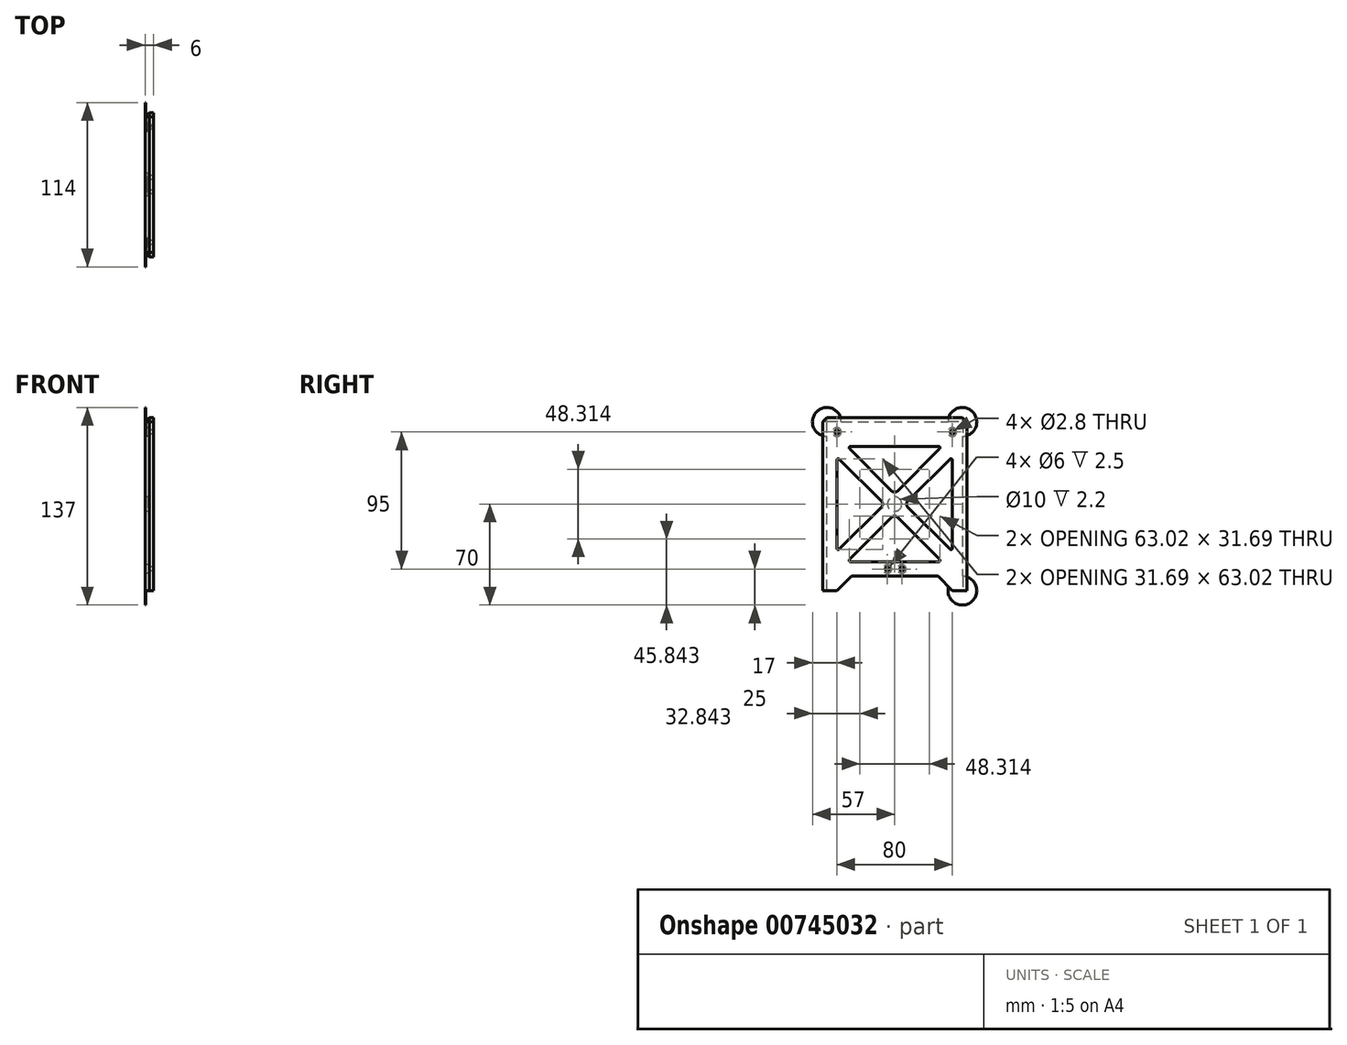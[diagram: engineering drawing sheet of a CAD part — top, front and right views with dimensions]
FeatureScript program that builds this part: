
annotation { "Feature Type Name" : "Feature", "Feature Type Description" : "" }
export const myFeature = defineFeature(function(context is Context, id is Id, definition is map)
    precondition{}
    {
        {
            var Q0;
            Q0=qCreatedBy(makeId("Right.planeOp"),FACE);
            var sketch = newSketch(context, id + "F0", { "sketchPlane" : qUnion([Q0])});
            skLineSegment(sketch, "E0.bottom", {"start": v(50, -60) * mm, "end": v(40.05, -60) * mm});
            skLineSegment(sketch, "E0.top", {"start": v(50, 60) * mm, "end": v(-50, 60) * mm});
            skLineSegment(sketch, "E0.left", {"start": v(50, -60) * mm, "end": v(50, 60) * mm});
            skLineSegment(sketch, "E0.right", {"start": v(-50, -60) * mm, "end": v(-50, 60) * mm});
            skPoint(sketch, "E0.middle", {"position": v(0, 0) * mm});
            skLineSegment(sketch, "E1.bottom", {"start": v(40, -40) * mm, "end": v(-32.93, -40) * mm});
            skLineSegment(sketch, "E1.top", {"start": v(32.93, 40) * mm, "end": v(-32.93, 40) * mm});
            skLineSegment(sketch, "E1.left", {"start": v(40, -40) * mm, "end": v(40, 32.93) * mm});
            skLineSegment(sketch, "E1.right", {"start": v(-40, -32.93) * mm, "end": v(-40, 32.93) * mm});
            skLineSegment(sketch, "E2.trimOffspring", {"start": v(-40, -60) * mm, "end": v(-50, -60) * mm});
            skLineSegment(sketch, "E3", {"start": v(30.05, -50) * mm, "end": v(40.05, -60) * mm});
            skLineSegment(sketch, "E4", {"start": v(30.05, -50) * mm, "end": v(-29.95, -50) * mm});
            skLineSegment(sketch, "E5", {"start": v(-29.95, -50) * mm, "end": v(-40, -60) * mm});
            skLineSegment(sketch, "E6", {"start": v(-40, -32.93) * mm, "end": v(-9.2, -2.12) * mm});
            skLineSegment(sketch, "E7.MirrorCS", {"start": v(-32.93, -40) * mm, "end": v(-2.12, -9.2) * mm});
            skLineSegment(sketch, "E8.trimOffspring", {"start": v(-40, 32.93) * mm, "end": v(-9.2, 2.12) * mm});
            skLineSegment(sketch, "E9.MirrorCS", {"start": v(-32.93, 40) * mm, "end": v(-2.12, 9.2) * mm});
            skLineSegment(sketch, "E10.trimOffspring", {"start": v(9.2, 2.12) * mm, "end": v(40, 32.93) * mm});
            skLineSegment(sketch, "E11.trimOffspring", {"start": v(2.12, -9.2) * mm, "end": v(32.93, -40) * mm});
            skLineSegment(sketch, "E12.trimOffspring", {"start": v(9.2, -2.12) * mm, "end": v(40, -32.93) * mm});
            skLineSegment(sketch, "E13.trimOffspring", {"start": v(2.12, 9.2) * mm, "end": v(32.93, 40) * mm});
            skPoint(sketch, "E14.visualSharp", {"position": v(0, 7.07) * mm});
            skArc(sketch, "E14.filletArc", {"start": v(-2.12, 9.2) * mm, "mid": v(0, 8.31) * mm, "end": v(2.12, 9.2) * mm});
            skPoint(sketch, "E15.visualSharp", {"position": v(0, -7.07) * mm});
            skArc(sketch, "E15.filletArc", {"start": v(2.12, -9.2) * mm, "mid": v(0, -8.31) * mm, "end": v(-2.12, -9.2) * mm});
            skPoint(sketch, "E16.visualSharp", {"position": v(7.07, 0) * mm});
            skArc(sketch, "E16.filletArc", {"start": v(9.2, 2.12) * mm, "mid": v(8.31, 0) * mm, "end": v(9.2, -2.12) * mm});
            skPoint(sketch, "E17.visualSharp", {"position": v(-7.07, 0) * mm});
            skArc(sketch, "E17.filletArc", {"start": v(-9.2, -2.12) * mm, "mid": v(-8.31, 0) * mm, "end": v(-9.2, 2.12) * mm});
            skLineSegment(sketch, "E18", {"start": v(81.83, 50) * mm, "end": v(-92.03, 50) * mm, "construction": true});
            skPoint(sketch, "E19", {"position": v(40, 50) * mm});
            skPoint(sketch, "E20", {"position": v(-40, 50) * mm});
            skSolve(sketch);
        }
        {
            var Q0;
            Q0=qSketchRegion(id+"F0",true);
            extrude(context, id + "F1", {"entities" : qUnion([Q0]), "depth" : 6 * mm, "offsetDistance" : 25 * mm});
        }
        {
            var Q0;
            Q0=makeQuery(id+"F1.opExtrude","SWEPT_EDGE",EDGE,{"disambiguationData":[OSD([sQuery(id+"F0.wireOp",EDGE,"E1.top"),sQuery(id+"F0.wireOp",EDGE,"E9.MirrorCS")])]});
            var Q1;
            Q1=makeQuery(id+"F1.opExtrude","SWEPT_EDGE",EDGE,{"disambiguationData":[OSD([sQuery(id+"F0.wireOp",EDGE,"E1.top"),sQuery(id+"F0.wireOp",EDGE,"E13.trimOffspring")])]});
            var Q2;
            Q2=makeQuery(id+"F1.opExtrude","SWEPT_EDGE",EDGE,{"disambiguationData":[OSD([sQuery(id+"F0.wireOp",EDGE,"E1.right"),sQuery(id+"F0.wireOp",EDGE,"E8.trimOffspring")])]});
            var Q3;
            Q3=makeQuery(id+"F1.opExtrude","SWEPT_EDGE",EDGE,{"disambiguationData":[OSD([sQuery(id+"F0.wireOp",EDGE,"E1.right"),sQuery(id+"F0.wireOp",EDGE,"E6")])]});
            var Q4;
            Q4=makeQuery(id+"F1.opExtrude","SWEPT_EDGE",EDGE,{"disambiguationData":[OSD([sQuery(id+"F0.wireOp",EDGE,"E1.bottom"),sQuery(id+"F0.wireOp",EDGE,"E7.MirrorCS")])]});
            var Q5;
            Q5=makeQuery(id+"F1.opExtrude","SWEPT_EDGE",EDGE,{"disambiguationData":[OSD([sQuery(id+"F0.wireOp",EDGE,"E1.left"),sQuery(id+"F0.wireOp",EDGE,"E10.trimOffspring")])]});
            var Q6;
            Q6=makeQuery(id+"F1.opExtrude","SWEPT_EDGE",EDGE,{"disambiguationData":[OSD([sQuery(id+"F0.wireOp",EDGE,"E1.left"),sQuery(id+"F0.wireOp",EDGE,"E12.trimOffspring")])]});
            var Q7;
            Q7=makeQuery(id+"F1.opExtrude","SWEPT_EDGE",EDGE,{"disambiguationData":[OSD([sQuery(id+"F0.wireOp",EDGE,"E1.bottom"),sQuery(id+"F0.wireOp",EDGE,"E11.trimOffspring")])]});
            fillet(context, id + "F2", {"entities" : qUnion([Q0, Q1, Q2, Q3, Q4, Q5, Q6, Q7]), "radius" : 1 * mm, "tangentPropagation" : true, "allowEdgeOverflow" : false});
        }
        {
            var Q0;
            Q0=sQuery(id+"F0.wireOp",VERTEX,"E20");
            var Q1;
            Q1=sQuery(id+"F0.wireOp",VERTEX,"E19");
            var Q2;
            Q2=makeQuery(id+"F1.opExtrude","SWEPT_BODY",BODY,{"disambiguationData":[OSD([sQuery(id+"F0.wireOp",EDGE,"E0.bottom"),sQuery(id+"F0.wireOp",EDGE,"E0.top"),sQuery(id+"F0.wireOp",EDGE,"E0.left"),sQuery(id+"F0.wireOp",EDGE,"E0.right"),sQuery(id+"F0.wireOp",EDGE,"E1.bottom"),sQuery(id+"F0.wireOp",EDGE,"E1.top"),sQuery(id+"F0.wireOp",EDGE,"E1.left"),sQuery(id+"F0.wireOp",EDGE,"E1.right"),sQuery(id+"F0.wireOp",EDGE,"E2.trimOffspring"),sQuery(id+"F0.wireOp",EDGE,"E3"),sQuery(id+"F0.wireOp",EDGE,"E4"),sQuery(id+"F0.wireOp",EDGE,"E5"),sQuery(id+"F0.wireOp",EDGE,"E6"),sQuery(id+"F0.wireOp",EDGE,"E7.MirrorCS"),sQuery(id+"F0.wireOp",EDGE,"E8.trimOffspring"),sQuery(id+"F0.wireOp",EDGE,"E9.MirrorCS"),sQuery(id+"F0.wireOp",EDGE,"E10.trimOffspring"),sQuery(id+"F0.wireOp",EDGE,"E11.trimOffspring"),sQuery(id+"F0.wireOp",EDGE,"E12.trimOffspring"),sQuery(id+"F0.wireOp",EDGE,"E13.trimOffspring"),sQuery(id+"F0.wireOp",EDGE,"E14.filletArc"),sQuery(id+"F0.wireOp",EDGE,"E15.filletArc"),sQuery(id+"F0.wireOp",EDGE,"E16.filletArc"),sQuery(id+"F0.wireOp",EDGE,"E17.filletArc")])]});
            hole(context, id + "F3", {"style" : HoleStyle.C_BORE, "endStyle" : HoleEndStyle.THROUGH, "oppositeDirection" : true, "holeDiameter" : 2.8 * mm, "cBoreDiameter" : 6 * mm, "cBoreDepth" : 2.5 * mm, "majorDiameter" : 5 * mm, "isTappedThrough" : true, "tappedDepth" : 6 * mm, "tapClearance" : 3, "locations" : qUnion([Q0, Q1]), "scope" : qUnion([Q2])});
        }
        {
            var Q0;
            Q0=makeQuery(id+"F1.opExtrude","CAP_FACE",FACE,{"disambiguationData":[OSD([sQuery(id+"F0.wireOp",EDGE,"E0.bottom"),sQuery(id+"F0.wireOp",EDGE,"E0.top"),sQuery(id+"F0.wireOp",EDGE,"E0.left"),sQuery(id+"F0.wireOp",EDGE,"E0.right"),sQuery(id+"F0.wireOp",EDGE,"E1.bottom"),sQuery(id+"F0.wireOp",EDGE,"E1.top"),sQuery(id+"F0.wireOp",EDGE,"E1.left"),sQuery(id+"F0.wireOp",EDGE,"E1.right"),sQuery(id+"F0.wireOp",EDGE,"E2.trimOffspring"),sQuery(id+"F0.wireOp",EDGE,"E3"),sQuery(id+"F0.wireOp",EDGE,"E4"),sQuery(id+"F0.wireOp",EDGE,"E5"),sQuery(id+"F0.wireOp",EDGE,"E6"),sQuery(id+"F0.wireOp",EDGE,"E7.MirrorCS"),sQuery(id+"F0.wireOp",EDGE,"E8.trimOffspring"),sQuery(id+"F0.wireOp",EDGE,"E9.MirrorCS"),sQuery(id+"F0.wireOp",EDGE,"E10.trimOffspring"),sQuery(id+"F0.wireOp",EDGE,"E11.trimOffspring"),sQuery(id+"F0.wireOp",EDGE,"E12.trimOffspring"),sQuery(id+"F0.wireOp",EDGE,"E13.trimOffspring"),sQuery(id+"F0.wireOp",EDGE,"E14.filletArc"),sQuery(id+"F0.wireOp",EDGE,"E15.filletArc"),sQuery(id+"F0.wireOp",EDGE,"E16.filletArc"),sQuery(id+"F0.wireOp",EDGE,"E17.filletArc")])],"isStart":true});
            var sketch = newSketch(context, id + "F4", { "sketchPlane" : qUnion([Q0])});
            skCircle(sketch, "E21", {"center": v(0, 0) * mm, "radius": 5 * mm});
            skSolve(sketch);
        }
        {
            var Q0;
            Q0=makeQuery(id+"F4.imprint","IMPRINT",FACE,{"disambiguationData":[TD([[makeQuery(id+"F4.imprint","IMPRINT",EDGE,{"derivedFrom":sQuery(id+"F4.wireOp",EDGE,"E21")}),1.0]])]});
            extrude(context, id + "F5", {"entities" : qUnion([Q0]), "operationType" : NewBodyOperationType.REMOVE, "oppositeDirection" : true, "depth" : 2.2 * mm, "offsetDistance" : 25 * mm});
        }
        {
            var Q0;
            {var subQ0=sQuery(id+"F0.wireOp",EDGE,"E0.left");var subQ1=sQuery(id+"F0.wireOp",EDGE,"E0.top");var subQ2=sQuery(id+"F0.wireOp",EDGE,"E0.right");var subQ3=sQuery(id+"F0.wireOp",EDGE,"E2.trimOffspring");var subQ4=sQuery(id+"F0.wireOp",EDGE,"E0.bottom");Q0=makeQuery(id+"F10.boolean.opBoolean","MERGE",FACE,{"derivedFrom":[makeQuery(id+"F1.opExtrude","CAP_FACE",FACE,{"disambiguationData":[OSD([subQ4,subQ1,subQ0,subQ2,sQuery(id+"F0.wireOp",EDGE,"E1.bottom"),sQuery(id+"F0.wireOp",EDGE,"E1.top"),sQuery(id+"F0.wireOp",EDGE,"E1.left"),sQuery(id+"F0.wireOp",EDGE,"E1.right"),subQ3,sQuery(id+"F0.wireOp",EDGE,"E3"),sQuery(id+"F0.wireOp",EDGE,"E4"),sQuery(id+"F0.wireOp",EDGE,"E5"),sQuery(id+"F0.wireOp",EDGE,"E6"),sQuery(id+"F0.wireOp",EDGE,"E7.MirrorCS"),sQuery(id+"F0.wireOp",EDGE,"E8.trimOffspring"),sQuery(id+"F0.wireOp",EDGE,"E9.MirrorCS"),sQuery(id+"F0.wireOp",EDGE,"E10.trimOffspring"),sQuery(id+"F0.wireOp",EDGE,"E11.trimOffspring"),sQuery(id+"F0.wireOp",EDGE,"E12.trimOffspring"),sQuery(id+"F0.wireOp",EDGE,"E13.trimOffspring"),sQuery(id+"F0.wireOp",EDGE,"E14.filletArc"),sQuery(id+"F0.wireOp",EDGE,"E15.filletArc"),sQuery(id+"F0.wireOp",EDGE,"E16.filletArc"),sQuery(id+"F0.wireOp",EDGE,"E17.filletArc")])],"isStart":true}),makeQuery(id+"F10.opExtrude","CAP_FACE",FACE,{"disambiguationData":[OSD([subQ4,subQ0,sQuery(id+"F9.wireOp",EDGE,"PSrgGkol-MO8q-g1fu-dDRE-y41ujJaxh7FT")])],"isStart":true}),makeQuery(id+"F10.opExtrude","CAP_FACE",FACE,{"disambiguationData":[OSD([subQ2,subQ3,sQuery(id+"F9.wireOp",EDGE,"1aKPLW1Y-IE5d-4tmK-5bFR-xkpx61fHem11")])],"isStart":true}),makeQuery(id+"F10.opExtrude","CAP_FACE",FACE,{"disambiguationData":[OSD([subQ1,subQ2,sQuery(id+"F9.wireOp",EDGE,"02GekRd3-WHB3-A6C6-mmOw-hFaiTY61e2sP")])],"isStart":true}),makeQuery(id+"F10.opExtrude","CAP_FACE",FACE,{"disambiguationData":[OSD([subQ1,subQ0,sQuery(id+"F9.wireOp",EDGE,"ECdukxah-RqsZ-JlNO-yzCW-vx4sxx8bxQE0")])],"isStart":true})]});}
            var sketch = newSketch(context, id + "F6", { "sketchPlane" : qUnion([Q0])});
            skPoint(sketch, "E22", {"position": v(-5, -45) * mm});
            skPoint(sketch, "E23.MirrorP", {"position": v(5, -45) * mm});
            skSolve(sketch);
        }
        {
            var Q0;
            Q0=sQuery(id+"F6.wireOp",VERTEX,"E22");
            var Q1;
            Q1=sQuery(id+"F6.wireOp",VERTEX,"E23.MirrorP");
            var Q2;
            Q2=makeQuery(id+"F1.opExtrude","SWEPT_BODY",BODY,{"disambiguationData":[OSD([sQuery(id+"F0.wireOp",EDGE,"E0.bottom"),sQuery(id+"F0.wireOp",EDGE,"E0.top"),sQuery(id+"F0.wireOp",EDGE,"E0.left"),sQuery(id+"F0.wireOp",EDGE,"E0.right"),sQuery(id+"F0.wireOp",EDGE,"E1.bottom"),sQuery(id+"F0.wireOp",EDGE,"E1.top"),sQuery(id+"F0.wireOp",EDGE,"E1.left"),sQuery(id+"F0.wireOp",EDGE,"E1.right"),sQuery(id+"F0.wireOp",EDGE,"E2.trimOffspring"),sQuery(id+"F0.wireOp",EDGE,"E3"),sQuery(id+"F0.wireOp",EDGE,"E4"),sQuery(id+"F0.wireOp",EDGE,"E5"),sQuery(id+"F0.wireOp",EDGE,"E6"),sQuery(id+"F0.wireOp",EDGE,"E7.MirrorCS"),sQuery(id+"F0.wireOp",EDGE,"E8.trimOffspring"),sQuery(id+"F0.wireOp",EDGE,"E9.MirrorCS"),sQuery(id+"F0.wireOp",EDGE,"E10.trimOffspring"),sQuery(id+"F0.wireOp",EDGE,"E11.trimOffspring"),sQuery(id+"F0.wireOp",EDGE,"E12.trimOffspring"),sQuery(id+"F0.wireOp",EDGE,"E13.trimOffspring"),sQuery(id+"F0.wireOp",EDGE,"E14.filletArc"),sQuery(id+"F0.wireOp",EDGE,"E15.filletArc"),sQuery(id+"F0.wireOp",EDGE,"E16.filletArc"),sQuery(id+"F0.wireOp",EDGE,"E17.filletArc")])]});
            hole(context, id + "F7", {"style" : HoleStyle.C_BORE, "endStyle" : HoleEndStyle.THROUGH, "holeDiameter" : 2.8 * mm, "cBoreDiameter" : 6 * mm, "cBoreDepth" : 2.5 * mm, "majorDiameter" : 5 * mm, "isTappedThrough" : true, "tappedDepth" : 6 * mm, "tapClearance" : 3, "locations" : qUnion([Q0, Q1]), "scope" : qUnion([Q2])});
        }
        {
            var Q0;
            Q0=makeQuery(id+"F1.opExtrude","SWEPT_EDGE",EDGE,{"disambiguationData":[OSD([sQuery(id+"F0.wireOp",EDGE,"E0.top"),sQuery(id+"F0.wireOp",EDGE,"E0.right")])]});
            var Q1;
            Q1=makeQuery(id+"F1.opExtrude","SWEPT_EDGE",EDGE,{"disambiguationData":[OSD([sQuery(id+"F0.wireOp",EDGE,"E0.top"),sQuery(id+"F0.wireOp",EDGE,"E0.left")])]});
            var Q2;
            Q2=makeQuery(id+"F1.opExtrude","CAP_EDGE",EDGE,{"disambiguationData":[OSD([sQuery(id+"F0.wireOp",EDGE,"E0.right")])],"isStart":true});
            var Q3;
            Q3=makeQuery(id+"F1.opExtrude","CAP_EDGE",EDGE,{"disambiguationData":[OSD([sQuery(id+"F0.wireOp",EDGE,"E0.left")])],"isStart":true});
            var Q4;
            Q4=makeQuery(id+"F1.opExtrude","CAP_EDGE",EDGE,{"disambiguationData":[OSD([sQuery(id+"F0.wireOp",EDGE,"E0.top")])],"isStart":true});
            chamfer(context, id + "F8", {"entities" : qUnion([Q0, Q1, Q2, Q3, Q4]), "width" : 3 * mm, "tangentPropagation" : true});
        }
        {
            var Q0;
            Q0=makeQuery(id+"F1.opExtrude","CAP_FACE",FACE,{"disambiguationData":[OSD([sQuery(id+"F0.wireOp",EDGE,"E0.bottom"),sQuery(id+"F0.wireOp",EDGE,"E0.top"),sQuery(id+"F0.wireOp",EDGE,"E0.left"),sQuery(id+"F0.wireOp",EDGE,"E0.right"),sQuery(id+"F0.wireOp",EDGE,"E1.bottom"),sQuery(id+"F0.wireOp",EDGE,"E1.top"),sQuery(id+"F0.wireOp",EDGE,"E1.left"),sQuery(id+"F0.wireOp",EDGE,"E1.right"),sQuery(id+"F0.wireOp",EDGE,"E2.trimOffspring"),sQuery(id+"F0.wireOp",EDGE,"E3"),sQuery(id+"F0.wireOp",EDGE,"E4"),sQuery(id+"F0.wireOp",EDGE,"E5"),sQuery(id+"F0.wireOp",EDGE,"E6"),sQuery(id+"F0.wireOp",EDGE,"E7.MirrorCS"),sQuery(id+"F0.wireOp",EDGE,"E8.trimOffspring"),sQuery(id+"F0.wireOp",EDGE,"E9.MirrorCS"),sQuery(id+"F0.wireOp",EDGE,"E10.trimOffspring"),sQuery(id+"F0.wireOp",EDGE,"E11.trimOffspring"),sQuery(id+"F0.wireOp",EDGE,"E12.trimOffspring"),sQuery(id+"F0.wireOp",EDGE,"E13.trimOffspring"),sQuery(id+"F0.wireOp",EDGE,"E14.filletArc"),sQuery(id+"F0.wireOp",EDGE,"E15.filletArc"),sQuery(id+"F0.wireOp",EDGE,"E16.filletArc"),sQuery(id+"F0.wireOp",EDGE,"E17.filletArc")])],"isStart":true});
            var sketch = newSketch(context, id + "F9", { "sketchPlane" : qUnion([Q0])});
            skPoint(sketch, "E24", {"position": v(-47, 57) * mm});
            skPoint(sketch, "E25", {"position": v(47, 57) * mm});
            skPoint(sketch, "E26", {"position": v(47, -60) * mm});
            skPoint(sketch, "E27", {"position": v(-47, -60) * mm});
            skArc(sketch, "E28", {"start": v(-37, 57) * mm, "mid": v(-54.07, 64.07) * mm, "end": v(-47, 47) * mm});
            skArc(sketch, "E29", {"start": v(47, 47) * mm, "mid": v(54.07, 64.07) * mm, "end": v(37, 57) * mm});
            skArc(sketch, "E30", {"start": v(47, -50) * mm, "mid": v(53.07, -67.95) * mm, "end": v(37.35, -57.37) * mm});
            skArc(sketch, "E31", {"start": v(-47, -50) * mm, "mid": v(-53.05, -67.96) * mm, "end": v(-37.37, -57.32) * mm});
            skSolve(sketch);
        }
        {
            var Q0;
            {var subQ0=sQuery(id+"F9.wireOp",EDGE,"E28");Q0=makeQuery(id+"F9.imprint","IMPRINT",FACE,{"disambiguationData":[TD([[makeQuery(id+"F9.imprint","IMPRINT",EDGE,{"derivedFrom":subQ0}),1.0]])]});}
            var Q1;
            {var subQ0=sQuery(id+"F9.wireOp",EDGE,"E29");Q1=makeQuery(id+"F9.imprint","IMPRINT",FACE,{"disambiguationData":[TD([[makeQuery(id+"F9.imprint","IMPRINT",EDGE,{"derivedFrom":subQ0}),1.0]])]});}
            var Q2;
            {var subQ0=sQuery(id+"F9.wireOp",EDGE,"E31");Q2=makeQuery(id+"F9.imprint","IMPRINT",FACE,{"disambiguationData":[TD([[makeQuery(id+"F9.imprint","IMPRINT",EDGE,{"derivedFrom":subQ0}),1.0]])]});}
            var Q3;
            {var subQ0=sQuery(id+"F9.wireOp",EDGE,"E30");Q3=makeQuery(id+"F9.imprint","IMPRINT",FACE,{"disambiguationData":[TD([[makeQuery(id+"F9.imprint","IMPRINT",EDGE,{"derivedFrom":subQ0}),-1.0]])]});}
            extrude(context, id + "F10", {"entities" : qUnion([Q0, Q1, Q2, Q3]), "operationType" : NewBodyOperationType.ADD, "oppositeDirection" : true, "depth" : 0.4 * mm, "offsetDistance" : 25 * mm});
        }
    });
